# Revit family: RUSHWORK_707_DN15-150.rfa
name_source: partatom
category: Арматура трубопроводов
units: mm (PartAtom-declared; Revit-internal decimal feet)

## family parameters
Всегда вертикально = Нет
На основе рабочей плоскости = Нет
Общий = Нет
При загрузке вырезать с полостями = Да
Размер круглого соединителя = Использовать диаметр
Тип детали = Нормальный

## types (11) — shared parameters
ADSK_Единица измерения = шт
ADSK_Завод-изготовитель = ООО "ТД "РАШВОРК"
URL = https://rwru.ru
Изготовитель = ООО "ТД "РАШВОРК"
Корпус = чугун GJL-250 (GG25)
zero-valued in all types: Отметка по умолчанию

## per-type parameters (varying)
| type | ADSK_Код изделия | ADSK_Масса | ADSK_Наименование | D | D1 | D2 | D3 | H2 | H3 | L | R | b | d | f | Соединитель | Тип ручки | Уго_длинна |
| Кран шаровой полнопроходной РАШВОРК 707-015-16, DN015, PN16, корпус - GJL-250 (GG25), шар - AISI304, уплотнение шара - PTFE, Ф/Ф | 707-015-16 | 1.7 | Кран шаровой полнопроходной РАШВОРК 707-015-16, DN015, PN16, корпус - GJL-250 (GG25), шар - AISI304, уплотнение шара - PTFE, Ф/Ф | 95 мм | 50 мм | 29 мм | 45 мм | 41 мм | 6 мм | 115 мм | 46 мм | 14 мм | 15 мм | 2 мм | 15 мм | Тип ручки : Тип 1 | 115 мм |
| Кран шаровой полнопроходной РАШВОРК 707-040-16, DN040, PN16, корпус - GJL-250 (GG25), шар - AISI304, уплотнение шара - PTFE, Ф/Ф | 707-040-16 | 7.5 | Кран шаровой полнопроходной РАШВОРК 707-040-16, DN040, PN16, корпус - GJL-250 (GG25), шар - AISI304, уплотнение шара - PTFE, Ф/Ф | 150 мм | 84 мм | 34 мм | 50 мм | 55 мм | 10 мм | 140 мм | 84 мм | 18 мм | 37 мм | 3 мм | 40 мм | Тип ручки : Тип 2 | 140 мм |
| Кран шаровой полнопроходной РАШВОРК 707-020-16, DN020, PN16, корпус - GJL-250 (GG25), шар - AISI304, уплотнение шара - PTFE, Ф/ | 707-020-16 | 2 | Кран шаровой полнопроходной РАШВОРК 707-020-16, DN020, PN16, корпус - GJL-250 (GG25), шар - AISI304, уплотнение шара - PTFE, Ф/Ф | 105 мм | 50 мм | 29 мм | 45 мм | 37 мм | 8 мм | 120 мм | 56 мм | 16 мм | 20 мм | 2 мм | 20 мм | Тип ручки : Тип 1 | 120 мм |
| Кран шаровой полнопроходной РАШВОРК 707-025-16, DN025, PN16, корпус - GJL-250 (GG25), шар - AISI304, уплотнение шара - PTFE, Ф/Ф | 707-025-16 | 2.1 | Кран шаровой полнопроходной РАШВОРК 707-025-16, DN025, PN16, корпус - GJL-250 (GG25), шар - AISI304, уплотнение шара - PTFE, Ф/Ф | 115 мм | 59 мм | 29 мм | 45 мм | 37 мм | 8 мм | 125 мм | 65 мм | 16 мм | 25 мм | 3 мм | 25 мм | Тип ручки : Тип 1 | 125 мм |
| Кран шаровой полнопроходной РАШВОРК 707-032-16, DN032, PN16, корпус - GJL-250 (GG25), шар - AISI304, уплотнение шара - PTFE, Ф/Ф | 707-032-16 | 5.9 | Кран шаровой полнопроходной РАШВОРК 707-032-16, DN032, PN16, корпус - GJL-250 (GG25), шар - AISI304, уплотнение шара - PTFE, Ф/Ф | 140 мм | 80 мм | 34 мм | 50 мм | 50 мм | 10 мм | 130 мм | 76 мм | 18 мм | 32 мм | 3 мм | 32 мм | Тип ручки : Тип 1 | 130 мм |
| Кран шаровой полнопроходной РАШВОРК 707-050-16, DN050, PN16, корпус - GJL-250 (GG25), шар - AISI304, уплотнение шара - PTFE, Ф/Ф | 707-050-16 | 8.5 | Кран шаровой полнопроходной РАШВОРК 707-050-16, DN050, PN16, корпус - GJL-250 (GG25), шар - AISI304, уплотнение шара - PTFE, Ф/Ф | 165 мм | 101 мм | 34 мм | 50 мм | 64 мм | 10 мм | 150 мм | 99 мм | 20 мм | 49 мм | 3 мм | 50 мм | Тип ручки : Тип 2 | 150 мм |
| Кран шаровой полнопроходной РАШВОРК 707-065-16, DN065, PN16, корпус - GJL-250 (GG25), шар - AISI304, уплотнение шара - PTFE, Ф/Ф | 707-065-16 | 13 | Кран шаровой полнопроходной РАШВОРК 707-065-16, DN065, PN16, корпус - GJL-250 (GG25), шар - AISI304, уплотнение шара - PTFE, Ф/Ф | 185 мм | 123 мм | 50 мм | 70 мм | 80 мм | 12 мм | 170 мм | 118 мм | 20 мм | 64 мм | 3 мм | 65 мм | Тип ручки : Тип 3 | 170 мм |
| Кран шаровой полнопроходной РАШВОРК 707-080-16, DN080, PN16, корпус - GJL-250 (GG25), шар - AISI304, уплотнение шара - PTFE, Ф/Ф | 707-080-16 | 20.5 | Кран шаровой полнопроходной РАШВОРК 707-080-16, DN080, PN16, корпус - GJL-250 (GG25), шар - AISI304, уплотнение шара - PTFE, Ф/Ф | 200 мм | 222 мм | 55 мм | 97 мм | 112 мм | 16 мм | 180 мм | 132 мм | 22 мм | 80 мм | 3 мм | 80 мм | Тип ручки : Тип 4 | 180 мм |
| Кран шаровой полнопроходной РАШВОРК 707-100-16, DN100, PN16, корпус - GJL-250 (GG25), шар - AISI304, уплотнение шара - PTFE, Ф/Ф | 707-100-16 | 28 | Кран шаровой полнопроходной РАШВОРК 707-100-16, DN100, PN16, корпус - GJL-250 (GG25), шар - AISI304, уплотнение шара - PTFE, Ф/Ф | 220 мм | 255 мм | 58 мм | 105 мм | 128 мм | 16 мм | 190 мм | 156 мм | 24 мм | 100 мм | 3 мм | 100 мм | Тип ручки : Тип 4 | 190 мм |
| Кран шаровой полнопроходной РАШВОРК 707-125-16, DN125, PN16, корпус - GJL-250 (GG25), шар - AISI304, уплотнение шара - PTFE, Ф/Ф | 707-125-16 | 49.5 | Кран шаровой полнопроходной РАШВОРК 707-125-16, DN125, PN16, корпус - GJL-250 (GG25), шар - AISI304, уплотнение шара - PTFE, Ф/Ф | 250 мм | 299 мм | 80 мм | 150 мм | 155 мм | 16 мм | 325 мм | 188 мм | 26 мм | 125 мм | 3 мм | 125 мм | Тип ручки : Тип 5 | 325 мм |
| Кран шаровой полнопроходной РАШВОРК 707-150-16, DN150, PN16, корпус - GJL-250 (GG25), шар - AISI304, уплотнение шара - PTFE, Ф/Ф | 707-150-16 | 67.5 | Кран шаровой полнопроходной РАШВОРК 707-150-16, DN150, PN16, корпус - GJL-250 (GG25), шар - AISI304, уплотнение шара - PTFE, Ф/Ф | 285 мм | 320 мм | 80 мм | 143 мм | 172 мм | 19 мм | 350 мм | 212 мм | 26 мм | 150 мм | 3 мм | 150 мм | Тип ручки : Тип 5 | 350 мм |
